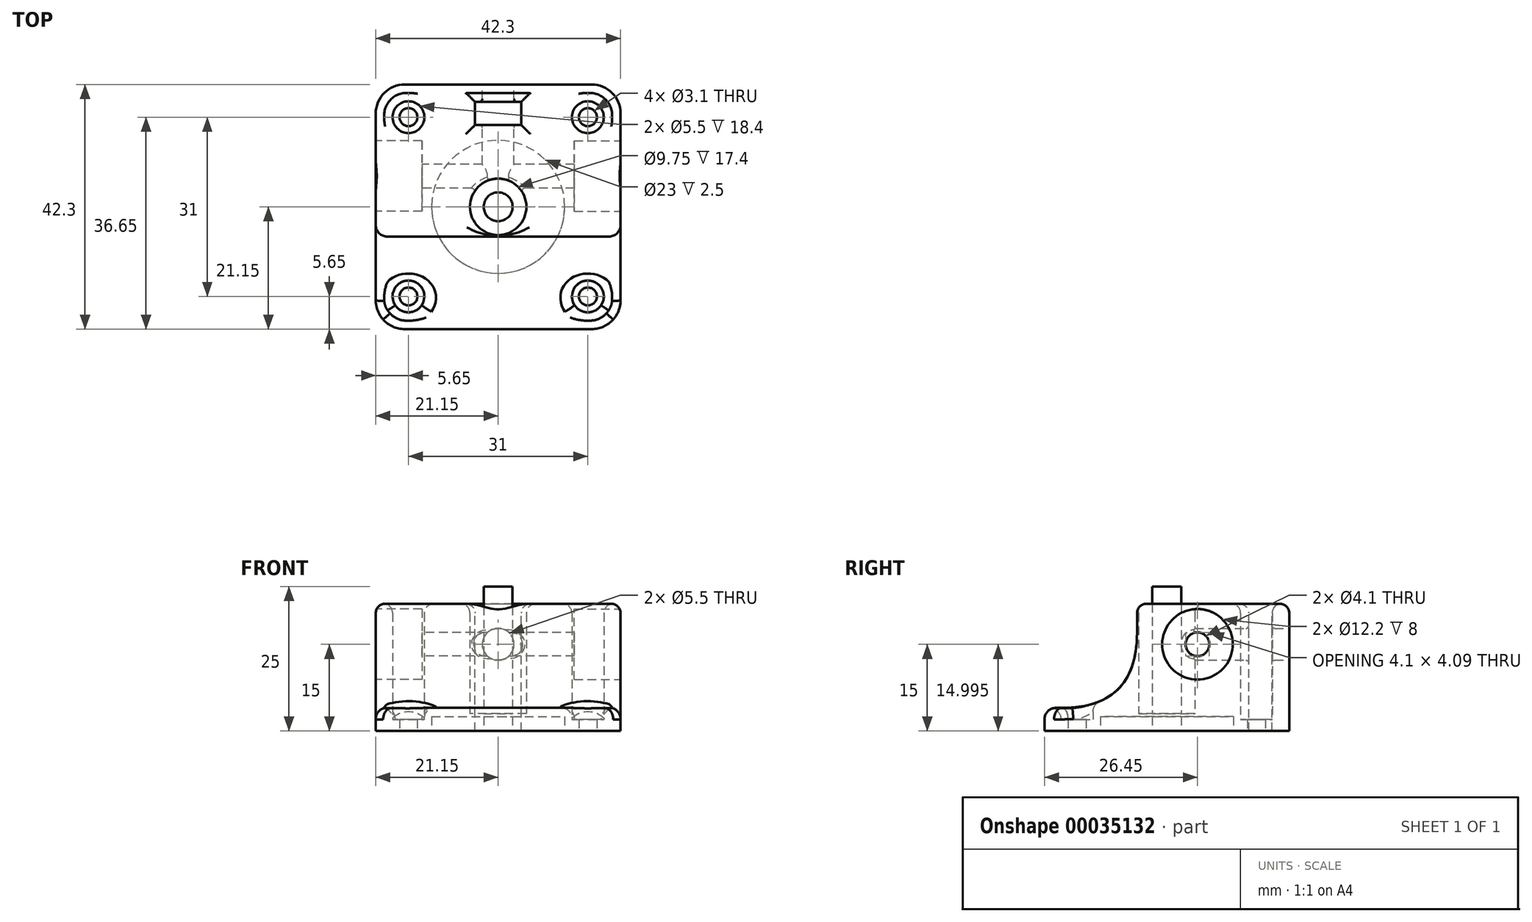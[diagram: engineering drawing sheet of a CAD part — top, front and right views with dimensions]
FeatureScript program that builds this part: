
annotation { "Feature Type Name" : "Feature", "Feature Type Description" : "" }
export const myFeature = defineFeature(function(context is Context, id is Id, definition is map)
    precondition{}
    {
        {
            var Q0;
            Q0=qCreatedBy(makeId("Top.planeOp"),FACE);
            var sketch = newSketch(context, id + "F0", { "sketchPlane" : qUnion([Q0])});
            skLineSegment(sketch, "E0.bottom", {"start": v(-21.15, 21.15) * mm, "end": v(21.15, 21.15) * mm});
            skLineSegment(sketch, "E0.top", {"start": v(-21.15, -21.15) * mm, "end": v(21.15, -21.15) * mm});
            skLineSegment(sketch, "E0.left", {"start": v(-21.15, 21.15) * mm, "end": v(-21.15, -21.15) * mm});
            skLineSegment(sketch, "E0.right", {"start": v(21.15, 21.15) * mm, "end": v(21.15, -21.15) * mm});
            skCircle(sketch, "E1", {"center": v(-15.5, 15.5) * mm, "radius": 1.55 * mm});
            skCircle(sketch, "E2", {"center": v(15.5, 15.5) * mm, "radius": 1.55 * mm});
            skCircle(sketch, "E3", {"center": v(15.5, -15.5) * mm, "radius": 1.55 * mm});
            skCircle(sketch, "E4", {"center": v(-15.5, -15.5) * mm, "radius": 1.55 * mm});
            skCircle(sketch, "E5", {"center": v(0, 0) * mm, "radius": 11.5 * mm});
            skSolve(sketch);
        }
        {
            var Q0;
            Q0=makeQuery(id+"F0.imprint","IMPRINT",FACE,{"disambiguationData":[TD([[makeQuery(id+"F0.imprint","IMPRINT",EDGE,{"derivedFrom":sQuery(id+"F0.wireOp",EDGE,"E0.bottom")}),-1.0]])]});
            extrude(context, id + "F1", {"entities" : qUnion([Q0]), "depth" : 2 * mm});
        }
        {
            var Q0;
            Q0=qCreatedBy(makeId("Top.planeOp"),FACE);
            var sketch = newSketch(context, id + "F2", { "sketchPlane" : qUnion([Q0])});
            skCircle(sketch, "E6", {"center": v(0, 0) * mm, "radius": 2.5 * mm});
            skSolve(sketch);
        }
        {
            var Q0;
            Q0=makeQuery(id+"F2.imprint","IMPRINT",FACE,{"disambiguationData":[TD([[makeQuery(id+"F2.imprint","IMPRINT",EDGE,{"derivedFrom":sQuery(id+"F2.wireOp",EDGE,"E6")}),1.0]])]});
            extrude(context, id + "F3", {"entities" : qUnion([Q0]), "depth" : 25 * mm});
        }
        {
            var Q0;
            Q0=makeQuery(id+"F1.opExtrude","CAP_FACE",FACE,{"disambiguationData":[OSD([sQuery(id+"F0.wireOp",EDGE,"E0.bottom"),sQuery(id+"F0.wireOp",EDGE,"E0.top"),sQuery(id+"F0.wireOp",EDGE,"E0.left"),sQuery(id+"F0.wireOp",EDGE,"E0.right"),sQuery(id+"F0.wireOp",EDGE,"E1"),sQuery(id+"F0.wireOp",EDGE,"E2"),sQuery(id+"F0.wireOp",EDGE,"E3"),sQuery(id+"F0.wireOp",EDGE,"E4"),sQuery(id+"F0.wireOp",EDGE,"E5")])],"isStart":false});
            var sketch = newSketch(context, id + "F4", { "sketchPlane" : qUnion([Q0])});
            skCircle(sketch, "E7", {"center": v(0, 0) * mm, "radius": 4.88 * mm});
            skCircle(sketch, "E8", {"center": v(-15.5, -15.5) * mm, "radius": 2.75 * mm});
            skCircle(sketch, "E9", {"center": v(15.5, -15.5) * mm, "radius": 2.75 * mm});
            skCircle(sketch, "E10", {"center": v(15.5, 15.5) * mm, "radius": 2.75 * mm});
            skCircle(sketch, "E11", {"center": v(-15.5, 15.5) * mm, "radius": 2.75 * mm});
            skSolve(sketch);
        }
        {
            var Q0;
            Q0=makeQuery(id+"F4.imprint","IMPRINT",FACE,{"disambiguationData":[TD([[makeQuery(id+"F4.imprint","IMPRINT",EDGE,{"derivedFrom":sQuery(id+"F4.wireOp",EDGE,"E7")}),-1.0]])]});
            var Q1;
            Q1=makeQuery(id+"F4.imprint","IMPRINT",FACE,{"disambiguationData":[TD([[makeQuery(id+"F4.imprint","IMPRINT",EDGE,{"derivedFrom":makeQuery(id+"F1.opExtrude","CAP_EDGE",EDGE,{"disambiguationData":[OSD([sQuery(id+"F0.wireOp",EDGE,"E0.bottom")])],"isStart":false})}),-1.0]])]});
            extrude(context, id + "F5", {"entities" : qUnion([Q0, Q1]), "operationType" : NewBodyOperationType.ADD, "depth" : 20 * mm});
        }
        {
            var Q0;
            Q0=qCreatedBy(makeId("Right.planeOp"),FACE);
            var sketch = newSketch(context, id + "F6", { "sketchPlane" : qUnion([Q0])});
            skCircle(sketch, "E12", {"center": v(5.3, 15) * mm, "radius": 2.05 * mm});
            skSolve(sketch);
        }
        {
            var Q0;
            Q0 = qSketchRegion(id + "F6", true);
            extrude(context, id + "F7", {"entities" : qUnion([Q0]), "operationType" : NewBodyOperationType.REMOVE, "depth" : 25 * mm, "hasSecondDirection" : true, "secondDirectionOppositeDirection" : true, "secondDirectionDepth" : 25 * mm});
        }
        {
            var Q0;
            Q0=makeQuery(id+"F5.opExtrude","CAP_FACE",FACE,{"disambiguationData":[OSD([sQuery(id+"F0.wireOp",EDGE,"E0.bottom"),sQuery(id+"F0.wireOp",EDGE,"E0.top"),sQuery(id+"F0.wireOp",EDGE,"E0.left"),sQuery(id+"F0.wireOp",EDGE,"E0.right"),sQuery(id+"F4.wireOp",EDGE,"E7"),sQuery(id+"F4.wireOp",EDGE,"E8"),sQuery(id+"F4.wireOp",EDGE,"E9"),sQuery(id+"F4.wireOp",EDGE,"E10"),sQuery(id+"F4.wireOp",EDGE,"E11")])],"isStart":false});
            var sketch = newSketch(context, id + "F8", { "sketchPlane" : qUnion([Q0])});
            skLineSegment(sketch, "E13.bottom", {"start": v(-4, 18.15) * mm, "end": v(4, 18.15) * mm});
            skLineSegment(sketch, "E13.top", {"start": v(-4, 14.15) * mm, "end": v(4, 14.15) * mm});
            skLineSegment(sketch, "E13.left", {"start": v(-4, 18.15) * mm, "end": v(-4, 14.15) * mm});
            skLineSegment(sketch, "E13.right", {"start": v(4, 18.15) * mm, "end": v(4, 14.15) * mm});
            skSolve(sketch);
        }
        {
            var Q0;
            Q0=makeQuery(id+"F8.imprint","IMPRINT",FACE,{"disambiguationData":[TD([[makeQuery(id+"F8.imprint","IMPRINT",EDGE,{"derivedFrom":sQuery(id+"F8.wireOp",EDGE,"E13.bottom")}),-1.0]])]});
            extrude(context, id + "F9", {"entities" : qUnion([Q0]), "operationType" : NewBodyOperationType.REMOVE, "oppositeDirection" : true, "depth" : 25 * mm});
        }
        {
            var Q0;
            {var subQ0=sQuery(id+"F0.wireOp",EDGE,"E0.bottom");Q0=makeQuery(id+"F5.boolean.opBoolean","MERGE",FACE,{"derivedFrom":[makeQuery(id+"F1.opExtrude","SWEPT_FACE",FACE,{"disambiguationData":[OSD([subQ0])]}),makeQuery(id+"F5.opExtrude","SWEPT_FACE",FACE,{"disambiguationData":[OSD([subQ0])]})]});}
            var sketch = newSketch(context, id + "F10", { "sketchPlane" : qUnion([Q0])});
            skCircle(sketch, "E14", {"center": v(0, 15) * mm, "radius": 2.75 * mm});
            skPoint(sketch, "E14.centerSnap0", {"position": v(0, 22) * mm});
            skSolve(sketch);
        }
        {
            var Q0;
            Q0 = qSketchRegion(id + "F10", true);
            var Q1;
            Q1=makeQuery(id+"F5.opExtrude","SWEPT_FACE",FACE,{"disambiguationData":[OSD([sQuery(id+"F4.wireOp",EDGE,"E7")])]});
            extrude(context, id + "F11", {"entities" : qUnion([Q0]), "operationType" : NewBodyOperationType.REMOVE, "endBound" : BoundingType.UP_TO_SURFACE, "oppositeDirection" : true, "endBoundEntityFace" : qUnion([Q1]), "depth" : 25 * mm});
        }
        {
            var Q0;
            {var subQ0=sQuery(id+"F0.wireOp",EDGE,"E0.left");Q0=makeQuery(id+"F5.boolean.opBoolean","MERGE",FACE,{"derivedFrom":[makeQuery(id+"F1.opExtrude","SWEPT_FACE",FACE,{"disambiguationData":[OSD([subQ0])]}),makeQuery(id+"F5.opExtrude","SWEPT_FACE",FACE,{"disambiguationData":[OSD([subQ0])]})]});}
            var sketch = newSketch(context, id + "F12", { "sketchPlane" : qUnion([Q0])});
            skCircle(sketch, "E15", {"center": v(-5.3, 15) * mm, "radius": 6.1 * mm});
            skSolve(sketch);
        }
        {
            var Q0;
            {var subQ0=sQuery(id+"F0.wireOp",EDGE,"E0.right");Q0=makeQuery(id+"F5.boolean.opBoolean","MERGE",FACE,{"derivedFrom":[makeQuery(id+"F1.opExtrude","SWEPT_FACE",FACE,{"disambiguationData":[OSD([subQ0])]}),makeQuery(id+"F5.opExtrude","SWEPT_FACE",FACE,{"disambiguationData":[OSD([subQ0])]})]});}
            var sketch = newSketch(context, id + "F13", { "sketchPlane" : qUnion([Q0])});
            skCircle(sketch, "E16", {"center": v(5.3, 15) * mm, "radius": 6.1 * mm});
            skSolve(sketch);
        }
        {
            var Q0;
            Q0=makeQuery(id+"F12.imprint","IMPRINT",FACE,{"disambiguationData":[TD([[makeQuery(id+"F12.imprint","IMPRINT",EDGE,{"derivedFrom":sQuery(id+"F12.wireOp",EDGE,"E15")}),1.0]])]});
            extrude(context, id + "F14", {"entities" : qUnion([Q0]), "operationType" : NewBodyOperationType.REMOVE, "oppositeDirection" : true, "depth" : 8 * mm});
        }
        {
            var Q0;
            Q0=makeQuery(id+"F13.imprint","IMPRINT",FACE,{"disambiguationData":[TD([[makeQuery(id+"F13.imprint","IMPRINT",EDGE,{"derivedFrom":sQuery(id+"F13.wireOp",EDGE,"E16")}),1.0]])]});
            extrude(context, id + "F15", {"entities" : qUnion([Q0]), "operationType" : NewBodyOperationType.REMOVE, "oppositeDirection" : true, "depth" : 8 * mm});
        }
        {
            var Q0;
            Q0=makeQuery(id+"F5.opExtrude","CAP_FACE",FACE,{"disambiguationData":[OSD([sQuery(id+"F0.wireOp",EDGE,"E0.bottom"),sQuery(id+"F0.wireOp",EDGE,"E0.top"),sQuery(id+"F0.wireOp",EDGE,"E0.left"),sQuery(id+"F0.wireOp",EDGE,"E0.right"),sQuery(id+"F4.wireOp",EDGE,"E7"),sQuery(id+"F4.wireOp",EDGE,"E8"),sQuery(id+"F4.wireOp",EDGE,"E9"),sQuery(id+"F4.wireOp",EDGE,"E10"),sQuery(id+"F4.wireOp",EDGE,"E11")])],"isStart":false});
            var sketch = newSketch(context, id + "F16", { "sketchPlane" : qUnion([Q0])});
            skLineSegment(sketch, "E17.bottom", {"start": v(-21.15, -5.15) * mm, "end": v(21.15, -5.15) * mm});
            skLineSegment(sketch, "E17.top", {"start": v(-21.15, -21.15) * mm, "end": v(21.15, -21.15) * mm});
            skLineSegment(sketch, "E17.left", {"start": v(-21.15, -5.15) * mm, "end": v(-21.15, -21.15) * mm});
            skLineSegment(sketch, "E17.right", {"start": v(21.15, -5.15) * mm, "end": v(21.15, -21.15) * mm});
            skSolve(sketch);
        }
        {
            var Q0;
            Q0=makeQuery(id+"F16.imprint","IMPRINT",FACE,{"disambiguationData":[TD([[makeQuery(id+"F16.imprint","IMPRINT",EDGE,{"derivedFrom":sQuery(id+"F16.wireOp",EDGE,"E17.bottom")}),-1.0]])]});
            extrude(context, id + "F17", {"entities" : qUnion([Q0]), "operationType" : NewBodyOperationType.REMOVE, "oppositeDirection" : true, "depth" : 18 * mm});
        }
        {
            var Q0;
            Q0=makeQuery(id+"F17.boolean.opBoolean","COPY",EDGE,{"derivedFrom":makeQuery(id+"F17.opExtrude","CAP_EDGE",EDGE,{"disambiguationData":[OSD([sQuery(id+"F16.wireOp",EDGE,"E17.bottom")])],"isStart":false})});
            fillet(context, id + "F18", {"entities" : qUnion([Q0]), "radius" : 13 * mm, "tangentPropagation" : true, "rho" : 0.5, "crossSection" : FilletCrossSection.CONIC, "allowEdgeOverflow" : false});
        }
        {
            var Q0;
            {var subQ0=sQuery(id+"F0.wireOp",EDGE,"E0.bottom");var subQ1=sQuery(id+"F0.wireOp",EDGE,"E0.right");Q0=makeQuery(id+"F5.boolean.opBoolean","MERGE",EDGE,{"derivedFrom":[makeQuery(id+"F1.opExtrude","SWEPT_EDGE",EDGE,{"disambiguationData":[OSD([subQ0,subQ1])]}),makeQuery(id+"F5.opExtrude","SWEPT_EDGE",EDGE,{"disambiguationData":[OSD([subQ0,subQ1])]})]});}
            var Q1;
            {var subQ0=sQuery(id+"F0.wireOp",EDGE,"E0.bottom");var subQ1=sQuery(id+"F0.wireOp",EDGE,"E0.left");Q1=makeQuery(id+"F5.boolean.opBoolean","MERGE",EDGE,{"derivedFrom":[makeQuery(id+"F1.opExtrude","SWEPT_EDGE",EDGE,{"disambiguationData":[OSD([subQ0,subQ1])]}),makeQuery(id+"F5.opExtrude","SWEPT_EDGE",EDGE,{"disambiguationData":[OSD([subQ0,subQ1])]})]});}
            var Q2;
            {var subQ0=sQuery(id+"F0.wireOp",EDGE,"E0.top");var subQ1=sQuery(id+"F0.wireOp",EDGE,"E0.right");Q2=makeQuery(id+"F5.boolean.opBoolean","MERGE",EDGE,{"derivedFrom":[makeQuery(id+"F1.opExtrude","SWEPT_EDGE",EDGE,{"disambiguationData":[OSD([subQ0,subQ1])]}),makeQuery(id+"F5.opExtrude","SWEPT_EDGE",EDGE,{"disambiguationData":[OSD([subQ0,subQ1])]})]});}
            var Q3;
            {var subQ0=sQuery(id+"F0.wireOp",EDGE,"E0.top");var subQ1=sQuery(id+"F0.wireOp",EDGE,"E0.left");Q3=makeQuery(id+"F5.boolean.opBoolean","MERGE",EDGE,{"derivedFrom":[makeQuery(id+"F1.opExtrude","SWEPT_EDGE",EDGE,{"disambiguationData":[OSD([subQ0,subQ1])]}),makeQuery(id+"F5.opExtrude","SWEPT_EDGE",EDGE,{"disambiguationData":[OSD([subQ0,subQ1])]})]});}
            fillet(context, id + "F19", {"entities" : qUnion([Q0, Q1, Q2, Q3]), "radius" : 5 * mm, "tangentPropagation" : true, "allowEdgeOverflow" : false});
        }
        {
            var Q0;
            Q0=makeQuery(id+"F18.opFillet","BLEND_FACE",FACE,{"disambiguationData":[OSD([sQuery(id+"F16.wireOp",EDGE,"E17.bottom")])]});
            fillet(context, id + "F20", {"entities" : qUnion([Q0]), "radius" : 2 * mm, "tangentPropagation" : true, "allowEdgeOverflow" : false});
        }
        {
            var Q0;
            Q0=makeQuery(id+"F15.boolean.opBoolean","COPY",EDGE,{"derivedFrom":makeQuery(id+"F15.opExtrude","CAP_EDGE",EDGE,{"disambiguationData":[OSD([sQuery(id+"F0.wireOp",EDGE,"E0.right"),sQuery(id+"F6.wireOp",EDGE,"E12")])],"isStart":false})});
            var Q1;
            Q1=makeQuery(id+"F14.boolean.opBoolean","COPY",EDGE,{"derivedFrom":makeQuery(id+"F14.opExtrude","CAP_EDGE",EDGE,{"disambiguationData":[OSD([sQuery(id+"F0.wireOp",EDGE,"E0.left"),sQuery(id+"F6.wireOp",EDGE,"E12")])],"isStart":false})});
            var Q2;
            Q2=makeQuery(id+"F11.boolean.opBoolean","SPLIT",EDGE,{"disambiguationData":[OD(0.0)],"derivedFrom":makeQuery(id+"F7.boolean.opBoolean","INTERSECT",EDGE,{"derivedFrom":[makeQuery(id+"F5.opExtrude","SWEPT_FACE",FACE,{"disambiguationData":[OSD([sQuery(id+"F4.wireOp",EDGE,"E7")])]}),makeQuery(id+"F7.opExtrude","SWEPT_FACE",FACE,{"disambiguationData":[OSD([sQuery(id+"F6.wireOp",EDGE,"E12")])]})]})});
            var Q3;
            Q3=makeQuery(id+"F11.boolean.opBoolean","SPLIT",EDGE,{"disambiguationData":[OD(1.0)],"derivedFrom":makeQuery(id+"F7.boolean.opBoolean","INTERSECT",EDGE,{"derivedFrom":[makeQuery(id+"F5.opExtrude","SWEPT_FACE",FACE,{"disambiguationData":[OSD([sQuery(id+"F4.wireOp",EDGE,"E7")])]}),makeQuery(id+"F7.opExtrude","SWEPT_FACE",FACE,{"disambiguationData":[OSD([sQuery(id+"F6.wireOp",EDGE,"E12")])]})]})});
            var Q4;
            Q4=makeQuery(id+"F11.boolean.opBoolean","COPY",EDGE,{"disambiguationData":[OD(1.0)],"derivedFrom":makeQuery(id+"F11.opExtrude","CAP_EDGE",EDGE,{"disambiguationData":[OSD([sQuery(id+"F10.wireOp",EDGE,"E14")])],"isStart":false})});
            var Q5;
            Q5=makeQuery(id+"F11.boolean.opBoolean","COPY",EDGE,{"disambiguationData":[OD(0.0)],"derivedFrom":makeQuery(id+"F11.opExtrude","CAP_EDGE",EDGE,{"disambiguationData":[OSD([sQuery(id+"F10.wireOp",EDGE,"E14")])],"isStart":false})});
            var Q6;
            Q6=makeQuery(id+"F11.boolean.opBoolean","COPY",EDGE,{"derivedFrom":makeQuery(id+"F11.opExtrude","CAP_EDGE",EDGE,{"disambiguationData":[OSD([sQuery(id+"F10.wireOp",EDGE,"E14")])],"isStart":true})});
            var Q7;
            Q7=makeQuery(id+"F11.boolean.opBoolean","INTERSECT",EDGE,{"derivedFrom":[makeQuery(id+"F9.boolean.opBoolean","COPY",FACE,{"derivedFrom":makeQuery(id+"F9.opExtrude","SWEPT_FACE",FACE,{"disambiguationData":[OSD([sQuery(id+"F8.wireOp",EDGE,"E13.bottom")])]})}),makeQuery(id+"F11.opExtrude","SWEPT_FACE",FACE,{"disambiguationData":[OSD([sQuery(id+"F10.wireOp",EDGE,"E14")])]})]});
            var Q8;
            Q8=makeQuery(id+"F11.boolean.opBoolean","INTERSECT",EDGE,{"derivedFrom":[makeQuery(id+"F9.boolean.opBoolean","COPY",FACE,{"derivedFrom":makeQuery(id+"F9.opExtrude","SWEPT_FACE",FACE,{"disambiguationData":[OSD([sQuery(id+"F8.wireOp",EDGE,"E13.top")])]})}),makeQuery(id+"F11.opExtrude","SWEPT_FACE",FACE,{"disambiguationData":[OSD([sQuery(id+"F10.wireOp",EDGE,"E14")])]})]});
            fillet(context, id + "F21", {"entities" : qUnion([Q0, Q1, Q2, Q3, Q4, Q5, Q6, Q7, Q8]), "radius" : 0.5 * mm, "tangentPropagation" : true, "allowEdgeOverflow" : false});
        }
        {
            var Q0;
            Q0=makeQuery(id+"F5.opExtrude","CAP_FACE",FACE,{"disambiguationData":[OSD([sQuery(id+"F0.wireOp",EDGE,"E0.bottom"),sQuery(id+"F0.wireOp",EDGE,"E0.top"),sQuery(id+"F0.wireOp",EDGE,"E0.left"),sQuery(id+"F0.wireOp",EDGE,"E0.right"),sQuery(id+"F4.wireOp",EDGE,"E7"),sQuery(id+"F4.wireOp",EDGE,"E8"),sQuery(id+"F4.wireOp",EDGE,"E9"),sQuery(id+"F4.wireOp",EDGE,"E10"),sQuery(id+"F4.wireOp",EDGE,"E11")])],"isStart":false});
            fillet(context, id + "F22", {"entities" : qUnion([Q0]), "radius" : 1.6 * mm, "allowEdgeOverflow" : false});
        }
        {
            var Q0;
            Q0=makeQuery(id+"F5.opExtrude","CAP_FACE",FACE,{"disambiguationData":[OSD([sQuery(id+"F0.wireOp",EDGE,"E0.bottom"),sQuery(id+"F0.wireOp",EDGE,"E0.top"),sQuery(id+"F0.wireOp",EDGE,"E0.left"),sQuery(id+"F0.wireOp",EDGE,"E0.right"),sQuery(id+"F4.wireOp",EDGE,"E7"),sQuery(id+"F4.wireOp",EDGE,"E8"),sQuery(id+"F4.wireOp",EDGE,"E9"),sQuery(id+"F4.wireOp",EDGE,"E10"),sQuery(id+"F4.wireOp",EDGE,"E11")])],"isStart":true});
            extrude(context, id + "F23", {"entities" : qUnion([Q0]), "operationType" : NewBodyOperationType.REMOVE, "oppositeDirection" : true, "depth" : 1 * mm});
        }
        {
            var Q0;
            Q0=makeQuery(id+"F23.boolean.opBoolean","COPY",FACE,{"derivedFrom":makeQuery(id+"F23.opExtrude","CAP_FACE",FACE,{"disambiguationData":[OSD([sQuery(id+"F0.wireOp",EDGE,"E0.bottom"),sQuery(id+"F0.wireOp",EDGE,"E0.top"),sQuery(id+"F0.wireOp",EDGE,"E0.left"),sQuery(id+"F0.wireOp",EDGE,"E0.right"),sQuery(id+"F4.wireOp",EDGE,"E7"),sQuery(id+"F4.wireOp",EDGE,"E8"),sQuery(id+"F4.wireOp",EDGE,"E9"),sQuery(id+"F4.wireOp",EDGE,"E10"),sQuery(id+"F4.wireOp",EDGE,"E11")])],"isStart":false})});
            var sketch = newSketch(context, id + "F24", { "sketchPlane" : qUnion([Q0])});
            skCircle(sketch, "E18", {"center": v(-0.42, 0) * mm, "radius": 12 * mm});
            skSolve(sketch);
        }
        {
            var Q0;
            Q0 = qSketchRegion(id + "F24", true);
            extrude(context, id + "F25", {"entities" : qUnion([Q0]), "operationType" : NewBodyOperationType.ADD, "depth" : 0.5 * mm});
        }
    });
